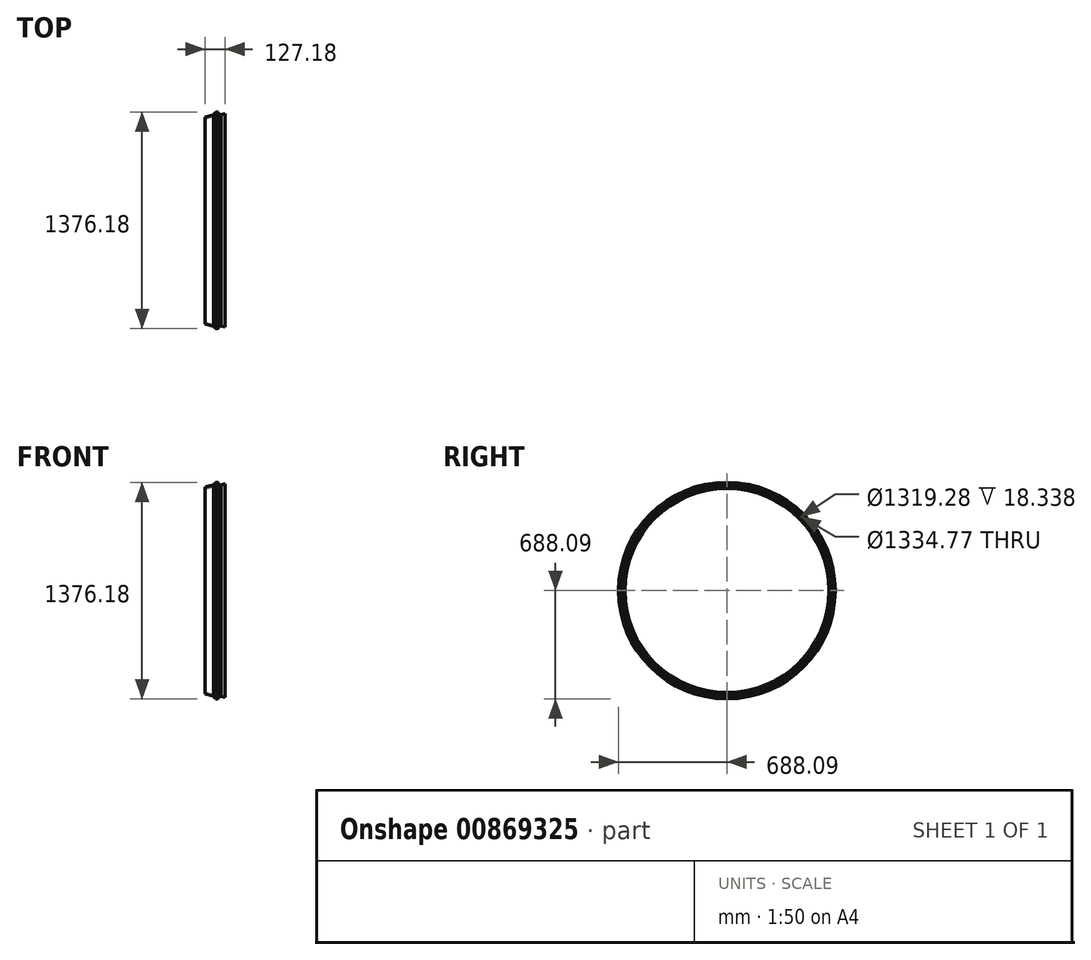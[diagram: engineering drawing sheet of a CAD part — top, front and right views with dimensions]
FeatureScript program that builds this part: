
annotation { "Feature Type Name" : "Feature", "Feature Type Description" : "" }
export const myFeature = defineFeature(function(context is Context, id is Id, definition is map)
    precondition{}
    {
        {
            var Q0;
            Q0=qCreatedBy(makeId("Front.planeOp"),FACE);
            var sketch = newSketch(context, id + "F0", { "sketchPlane" : qUnion([Q0])});
            skLineSegment(sketch, "E0", {"start": v(0, 687.96) * mm, "end": v(0, 672.7) * mm});
            skLineSegment(sketch, "E1", {"start": v(0.83, 665) * mm, "end": v(-9.05, 665) * mm});
            skLineSegment(sketch, "E2", {"start": v(-9.05, 665) * mm, "end": v(-10.67, 663.38) * mm});
            skLineSegment(sketch, "E3", {"start": v(-10.67, 663.38) * mm, "end": v(-10.67, 659.64) * mm});
            skLineSegment(sketch, "E4", {"start": v(-10.67, 659.64) * mm, "end": v(7.67, 659.64) * mm});
            skLineSegment(sketch, "E5", {"start": v(23.83, 664.58) * mm, "end": v(7.67, 659.64) * mm});
            skLineSegment(sketch, "E6", {"start": v(25.6, 667.84) * mm, "end": v(51.82, 674.52) * mm});
            skLineSegment(sketch, "E7", {"start": v(26.51, 671.35) * mm, "end": v(15.07, 671.35) * mm});
            skLineSegment(sketch, "E8", {"start": v(0, 687.96) * mm, "end": v(4.3, 687.96) * mm});
            skLineSegment(sketch, "E9", {"start": v(6.17, 686.74) * mm, "end": v(10.3, 675.41) * mm});
            skArc(sketch, "E10", {"start": v(4.3, 687.96) * mm, "mid": v(5.42, 687.63) * mm, "end": v(6.17, 686.74) * mm});
            skArc(sketch, "E11", {"start": v(10.3, 675.41) * mm, "mid": v(12.14, 672.75) * mm, "end": v(15.07, 671.35) * mm});
            skArc(sketch, "E12", {"start": v(25.6, 667.84) * mm, "mid": v(24, 666.6) * mm, "end": v(23.83, 664.58) * mm});
            skArc(sketch, "E13", {"start": v(0, 672.7) * mm, "mid": v(0.23, 671.9) * mm, "end": v(0.83, 671.35) * mm});
            skArc(sketch, "E14", {"start": v(0.83, 665) * mm, "mid": v(4, 668.17) * mm, "end": v(0.83, 671.35) * mm});
            skPoint(sketch, "E15", {"position": v(8.23, 681.08) * mm});
            skLineSegment(sketch, "E16", {"start": v(51.82, 674.52) * mm, "end": v(51.82, 677.8) * mm});
            skLineSegment(sketch, "E17", {"start": v(51.82, 677.8) * mm, "end": v(26.51, 671.35) * mm});
            skPoint(sketch, "E18", {"position": v(15.75, 662.1) * mm});
            skSolve(sketch);
        }
        {
            var Q0;
            Q0=qCreatedBy(makeId("Front.planeOp"),FACE);
            var sketch = newSketch(context, id + "F1", { "sketchPlane" : qUnion([Q0])});
            skLineSegment(sketch, "E19", {"start": v(-1.27, 687.96) * mm, "end": v(-6.99, 687.96) * mm});
            skLineSegment(sketch, "E20", {"start": v(-1.27, 687.96) * mm, "end": v(-1.27, 670.17) * mm});
            skLineSegment(sketch, "E21", {"start": v(-1.27, 670.17) * mm, "end": v(-6.1, 667.39) * mm});
            skLineSegment(sketch, "E22", {"start": v(-6.1, 667.39) * mm, "end": v(-11.96, 667.39) * mm});
            skLineSegment(sketch, "E23", {"start": v(-14.48, 664.52) * mm, "end": v(-14.48, 662.18) * mm});
            skLineSegment(sketch, "E24", {"start": v(-14.48, 662.18) * mm, "end": v(-73.11, 648.35) * mm});
            skLineSegment(sketch, "E25", {"start": v(-73.11, 648.35) * mm, "end": v(-75.36, 657.88) * mm});
            skLineSegment(sketch, "E26", {"start": v(-75.36, 657.88) * mm, "end": v(-26.8, 669.34) * mm});
            skLineSegment(sketch, "E27", {"start": v(-8, 686.69) * mm, "end": v(-10.76, 679.12) * mm});
            skLineSegment(sketch, "E28", {"start": v(-12.45, 677.8) * mm, "end": v(-20, 677.8) * mm});
            skArc(sketch, "E29", {"start": v(-26.8, 669.34) * mm, "mid": v(-21.94, 672.4) * mm, "end": v(-20, 677.8) * mm});
            skArc(sketch, "E30", {"start": v(-10.76, 679.12) * mm, "mid": v(-11.41, 678.22) * mm, "end": v(-12.45, 677.8) * mm});
            skArc(sketch, "E31", {"start": v(-8, 686.69) * mm, "mid": v(-7.6, 687.4) * mm, "end": v(-6.98, 687.96) * mm});
            skArc(sketch, "E32", {"start": v(-11.96, 667.39) * mm, "mid": v(-13.87, 666.52) * mm, "end": v(-14.48, 664.52) * mm});
            skSolve(sketch);
        }
        {
            var Q0;
            Q0=qCreatedBy(makeId("Front.planeOp"),FACE);
            var sketch = newSketch(context, id + "F2", { "sketchPlane" : qUnion([Q0])});
            skLineSegment(sketch, "E33", {"start": v(-40.07, 0) * mm, "end": v(63.9, 0) * mm});
            skSolve(sketch);
        }
        {
            var Q0;
            Q0=makeQuery(id+"F1.imprint","IMPRINT",FACE,{"disambiguationData":[TD([[makeQuery(id+"F1.imprint","IMPRINT",EDGE,{"derivedFrom":sQuery(id+"F1.wireOp",EDGE,"E19")}),1.0]])]});
            var Q1;
            Q1=makeQuery(id+"F0.imprint","IMPRINT",FACE,{"disambiguationData":[TD([[makeQuery(id+"F0.imprint","IMPRINT",EDGE,{"derivedFrom":sQuery(id+"F0.wireOp",EDGE,"E0")}),1.0]])]});
            var Q2;
            Q2=sQuery(id+"F2.wireOp",EDGE,"E33");
            revolve(context, id + "F3", {"surfaceOperationType" : NewSurfaceOperationType.NEW, "entities" : qUnion([Q0, Q1]), "axis" : qUnion([Q2]), "revolveType" : RevolveType.FULL});
        }
        {
            var Q0;
            Q0=qCreatedBy(makeId("Front.planeOp"),FACE);
            var sketch = newSketch(context, id + "F4", { "sketchPlane" : qUnion([Q0])});
            skLineSegment(sketch, "E34", {"start": v(-1.37, 688.09) * mm, "end": v(1.8, 688.09) * mm});
            skLineSegment(sketch, "E35", {"start": v(-1.37, 688.09) * mm, "end": v(-1.37, 673.1) * mm});
            skLineSegment(sketch, "E36", {"start": v(-1.37, 673.1) * mm, "end": v(1.8, 673.1) * mm});
            skLineSegment(sketch, "E37", {"start": v(1.8, 688.09) * mm, "end": v(1.8, 673.1) * mm});
            skSolve(sketch);
        }
        {
            var Q0;
            Q0=makeQuery(id+"F4.imprint","IMPRINT",FACE,{"disambiguationData":[TD([[makeQuery(id+"F4.imprint","IMPRINT",EDGE,{"derivedFrom":sQuery(id+"F4.wireOp",EDGE,"E34")}),-1.0]])]});
            extrude(context, id + "F5", {"entities" : qUnion([Q0]), "endBound" : BoundingType.SYMMETRIC, "depth" : 3.17 * mm, "offsetDistance" : 25.4 * mm});
        }
        {
            var Q0;
            Q0=makeQuery(id+"F5.opExtrude","SWEPT_BODY",BODY,{"disambiguationData":[OSD([sQuery(id+"F4.wireOp",EDGE,"E34"),sQuery(id+"F4.wireOp",EDGE,"E35"),sQuery(id+"F4.wireOp",EDGE,"E36"),sQuery(id+"F4.wireOp",EDGE,"E37")])]});
            var Q1;
            Q1=makeQuery(id+"F3.opRevolve","SWEPT_EDGE",EDGE,{"disambiguationData":[OSD([sQuery(id+"F0.wireOp",EDGE,"E0"),sQuery(id+"F0.wireOp",EDGE,"E8")])]});
            circularPattern(context, id + "F6", {"entities" : qUnion([Q0]), "axis" : qUnion([Q1]), "angle" : 360 * degree, "instanceCount" : 12, "equalSpace" : true});
        }
    });
